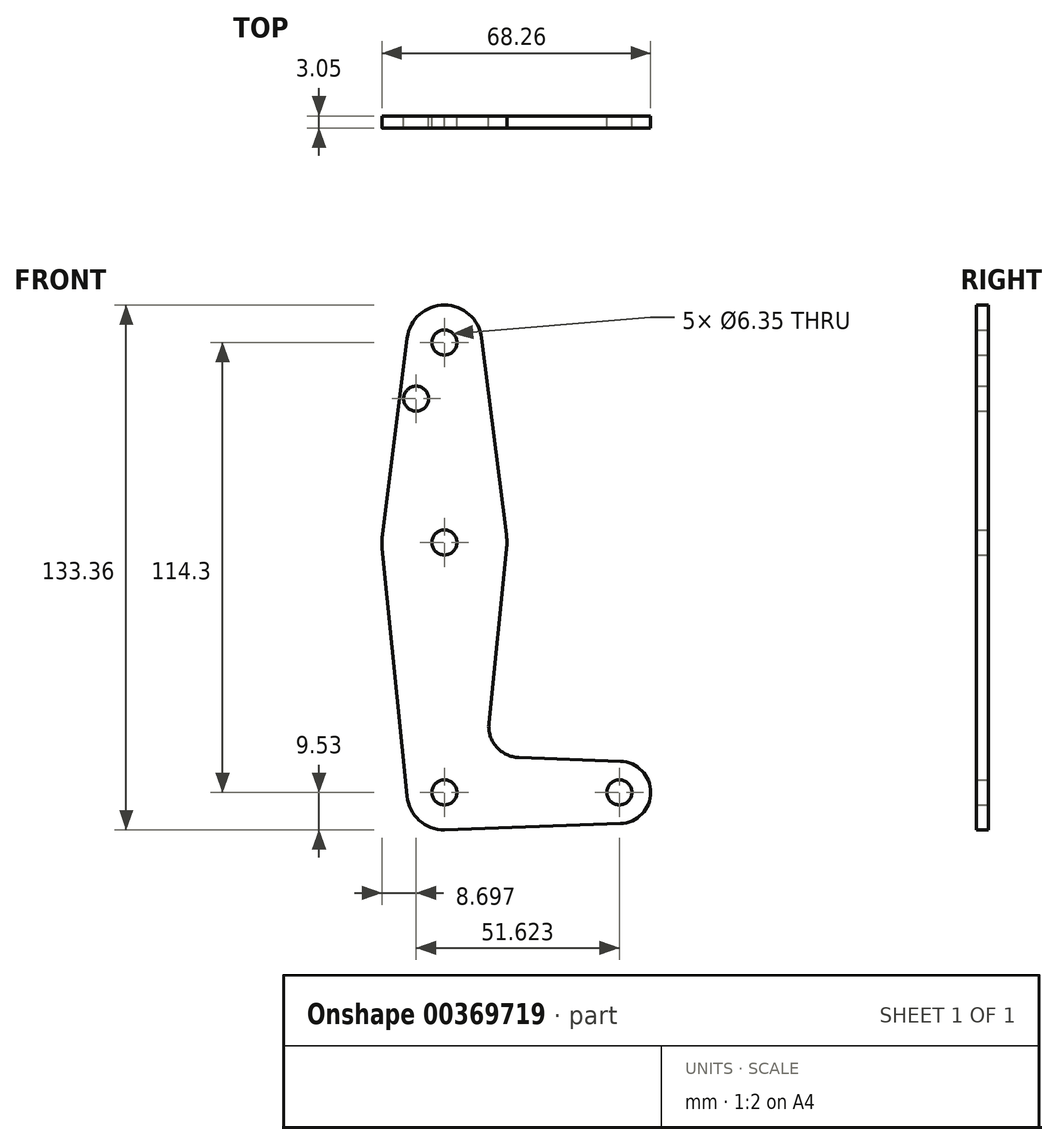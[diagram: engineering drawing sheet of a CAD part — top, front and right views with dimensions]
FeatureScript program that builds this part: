
annotation { "Feature Type Name" : "Feature", "Feature Type Description" : "" }
export const myFeature = defineFeature(function(context is Context, id is Id, definition is map)
    precondition{}
    {
        {
            var Q0;
            Q0=qCreatedBy(makeId("Front.planeOp"),FACE);
            var sketch = newSketch(context, id + "F0", { "sketchPlane" : qUnion([Q0])});
            skLineSegment(sketch, "E0", {"start": v(0, 0) * mm, "end": v(0, 114.3) * mm});
            skLineSegment(sketch, "E1", {"start": v(44.45, 0) * mm, "end": v(0, 0) * mm});
            skCircle(sketch, "E2", {"center": v(0, 114.3) * mm, "radius": 9.52 * mm});
            skCircle(sketch, "E3", {"center": v(0, 63.5) * mm, "radius": 15.88 * mm});
            skCircle(sketch, "E4", {"center": v(0, 0) * mm, "radius": 9.52 * mm});
            skCircle(sketch, "E5", {"center": v(44.45, 0) * mm, "radius": 7.94 * mm});
            skLineSegment(sketch, "E6", {"start": v(9.45, 115.5) * mm, "end": v(15.98, 63.7) * mm});
            skLineSegment(sketch, "E7", {"start": v(-15.75, 65.48) * mm, "end": v(-9.45, 115.5) * mm});
            skLineSegment(sketch, "E8", {"start": v(11.3, 17.6) * mm, "end": v(15.98, 63.7) * mm});
            skLineSegment(sketch, "E9", {"start": v(0, -9.52) * mm, "end": v(44.73, -7.93) * mm});
            skLineSegment(sketch, "E10", {"start": v(18.93, 8.85) * mm, "end": v(44.73, 7.93) * mm});
            skCircle(sketch, "E11", {"center": v(0, 114.3) * mm, "radius": 3.18 * mm});
            skCircle(sketch, "E12", {"center": v(0, 63.5) * mm, "radius": 3.18 * mm});
            skCircle(sketch, "E13", {"center": v(0, 0) * mm, "radius": 3.18 * mm});
            skCircle(sketch, "E14", {"center": v(44.45, 0) * mm, "radius": 3.18 * mm});
            skPoint(sketch, "E15.newPointB", {"position": v(0, 9.52) * mm});
            skArc(sketch, "E15.filletArc", {"start": v(11.3, 17.6) * mm, "mid": v(13.22, 11.57) * mm, "end": v(18.93, 8.85) * mm});
            skCircle(sketch, "E16", {"center": v(-7.17, 100.03) * mm, "radius": 3.18 * mm});
            skLineSegment(sketch, "E17", {"start": v(-15.8, 61.91) * mm, "end": v(-9.48, -0.95) * mm});
            skSolve(sketch);
        }
        {
            var Q0;
            Q0=makeQuery(id+"F0.imprint","IMPRINT",FACE,{"disambiguationData":[TD([[makeQuery(id+"F0.imprint","IMPRINT",EDGE,{"derivedFrom":sQuery(id+"F0.wireOp",EDGE,"E11")}),-1.0]])]});
            var Q1;
            {var subQ0=sQuery(id+"F0.wireOp",EDGE,"E2");var subQ1=sQuery(id+"F0.wireOp",EDGE,"E0");var subQ2=makeQuery(id+"F0.imprint","INTERSECT",VERTEX,{"derivedFrom":[subQ1,subQ0]});Q1=makeQuery(id+"F0.imprint","IMPRINT",FACE,{"disambiguationData":[TD([[makeQuery(id+"F0.imprint","IMPRINT",EDGE,{"disambiguationData":[TD([[subQ2,1.0]])],"derivedFrom":subQ1}),-1.0]])]});}
            var Q2;
            {var subQ0=sQuery(id+"F0.wireOp",EDGE,"E7");Q2=makeQuery(id+"F0.imprint","IMPRINT",FACE,{"disambiguationData":[TD([[makeQuery(id+"F0.imprint","IMPRINT",EDGE,{"derivedFrom":subQ0}),-1.0]])]});}
            var Q3;
            {var subQ0=sQuery(id+"F0.wireOp",EDGE,"E3");var subQ2=sQuery(id+"F0.wireOp",EDGE,"E0");var subQ4=makeQuery(id+"F0.imprint","INTERSECT",VERTEX,{"disambiguationData":[OD(0.0)],"derivedFrom":[subQ2,subQ0]});Q3=makeQuery(id+"F0.imprint","IMPRINT",FACE,{"disambiguationData":[TD([[makeQuery(id+"F0.imprint","IMPRINT",EDGE,{"disambiguationData":[TD([[subQ4,-1.0]])],"derivedFrom":subQ2}),1.0]])]});}
            var Q4;
            {var subQ0=sQuery(id+"F0.wireOp",EDGE,"E3");var subQ2=sQuery(id+"F0.wireOp",EDGE,"E0");var subQ3=makeQuery(id+"F0.imprint","INTERSECT",VERTEX,{"disambiguationData":[OD(0.0)],"derivedFrom":[subQ2,subQ0]});Q4=makeQuery(id+"F0.imprint","IMPRINT",FACE,{"disambiguationData":[TD([[makeQuery(id+"F0.imprint","IMPRINT",EDGE,{"disambiguationData":[TD([[subQ3,-1.0]])],"derivedFrom":subQ2}),-1.0]])]});}
            var Q5;
            {var subQ12=sQuery(id+"F0.wireOp",EDGE,"E10");Q5=makeQuery(id+"F0.imprint","IMPRINT",FACE,{"disambiguationData":[TD([[makeQuery(id+"F0.imprint","IMPRINT",EDGE,{"derivedFrom":subQ12}),-1.0]])]});}
            var Q6;
            {var subQ5=sQuery(id+"F0.wireOp",EDGE,"E17");Q6=makeQuery(id+"F0.imprint","IMPRINT",FACE,{"disambiguationData":[TD([[makeQuery(id+"F0.imprint","IMPRINT",EDGE,{"derivedFrom":subQ5}),1.0]])]});}
            var Q7;
            {var subQ2=sQuery(id+"F0.wireOp",EDGE,"E0");var subQ6=sQuery(id+"F0.wireOp",EDGE,"E13");var subQ11=makeQuery(id+"F0.imprint","INTERSECT",VERTEX,{"derivedFrom":[subQ2,subQ6]});Q7=makeQuery(id+"F0.imprint","IMPRINT",FACE,{"disambiguationData":[TD([[makeQuery(id+"F0.imprint","IMPRINT",EDGE,{"disambiguationData":[TD([[subQ11,-1.0]])],"derivedFrom":subQ2}),1.0]])]});}
            var Q8;
            {var subQ0=sQuery(id+"F0.wireOp",EDGE,"E13");var subQ1=sQuery(id+"F0.wireOp",EDGE,"E0");var subQ2=makeQuery(id+"F0.imprint","INTERSECT",VERTEX,{"derivedFrom":[subQ1,subQ0]});Q8=makeQuery(id+"F0.imprint","IMPRINT",FACE,{"disambiguationData":[TD([[makeQuery(id+"F0.imprint","IMPRINT",EDGE,{"disambiguationData":[TD([[subQ2,-1.0]])],"derivedFrom":subQ1}),-1.0]])]});}
            var Q9;
            {var subQ0=sQuery(id+"F0.wireOp",EDGE,"E5");var subQ1=sQuery(id+"F0.wireOp",EDGE,"E1");var subQ2=makeQuery(id+"F0.imprint","INTERSECT",VERTEX,{"derivedFrom":[subQ1,subQ0]});Q9=makeQuery(id+"F0.imprint","IMPRINT",FACE,{"disambiguationData":[TD([[makeQuery(id+"F0.imprint","IMPRINT",EDGE,{"disambiguationData":[TD([[subQ2,-1.0]])],"derivedFrom":subQ1}),1.0]])]});}
            var Q10;
            Q10=makeQuery(id+"F0.imprint","IMPRINT",FACE,{"disambiguationData":[TD([[makeQuery(id+"F0.imprint","IMPRINT",EDGE,{"derivedFrom":sQuery(id+"F0.wireOp",EDGE,"E14")}),-1.0]])]});
            extrude(context, id + "F1", {"entities" : qUnion([Q0, Q1, Q2, Q3, Q4, Q5, Q6, Q7, Q8, Q9, Q10]), "depth" : 3.05 * mm});
        }
    });
